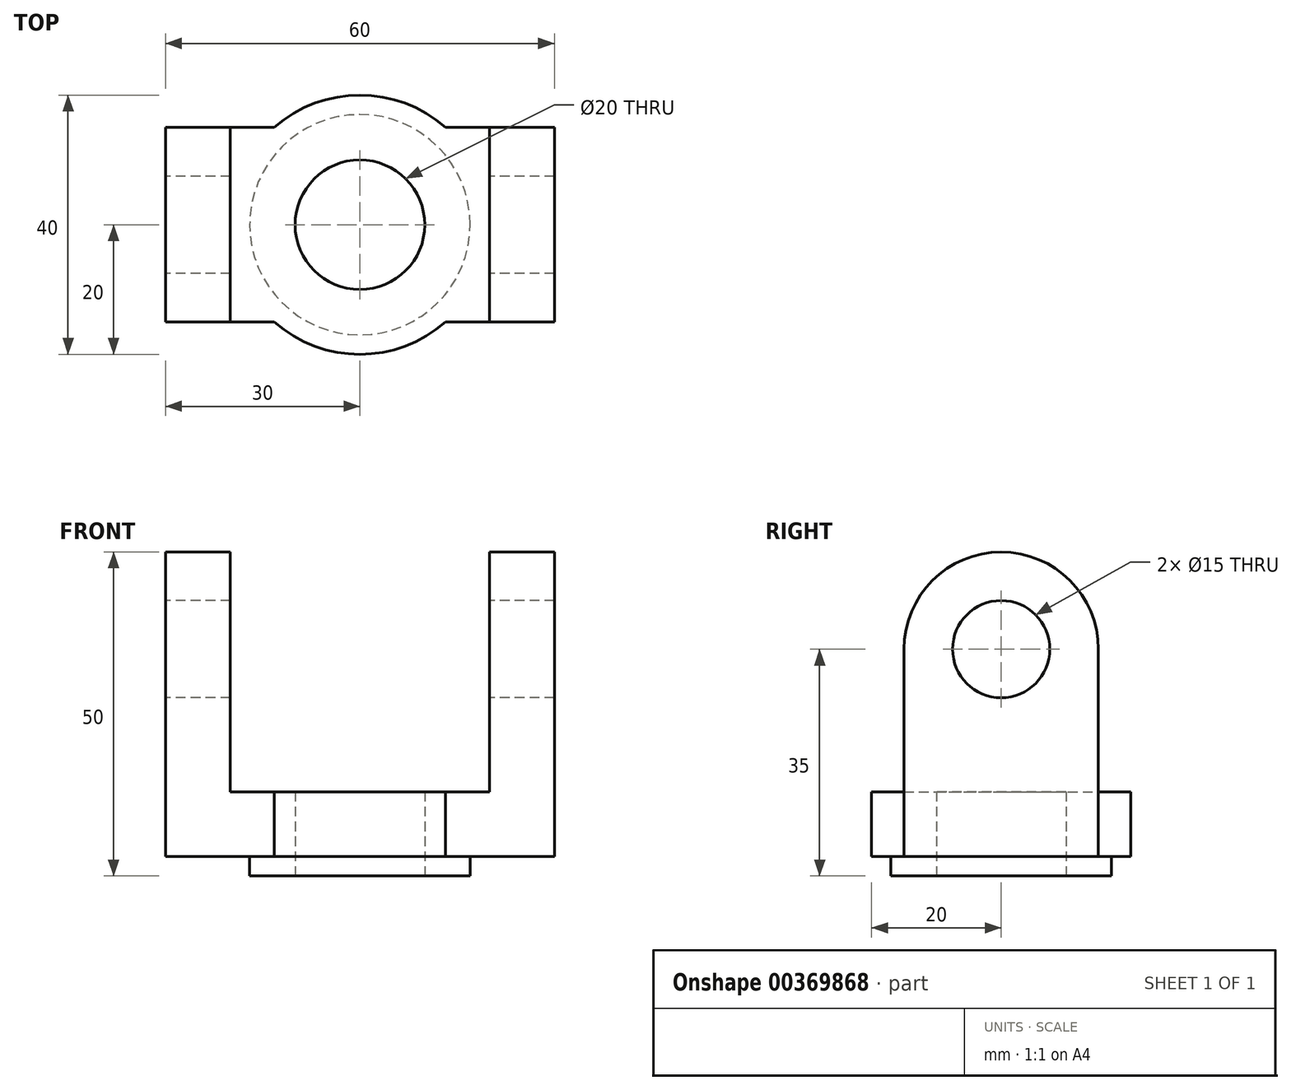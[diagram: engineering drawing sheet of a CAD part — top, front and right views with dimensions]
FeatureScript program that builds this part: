
annotation { "Feature Type Name" : "Feature", "Feature Type Description" : "" }
export const myFeature = defineFeature(function(context is Context, id is Id, definition is map)
    precondition{}
    {
        {
            var Q0;
            Q0=qCreatedBy(makeId("Top.planeOp"),FACE);
            var sketch = newSketch(context, id + "F0", { "sketchPlane" : qUnion([Q0])});
            skLineSegment(sketch, "E0.bottom", {"start": v(-30, 15) * mm, "end": v(-13.23, 15) * mm});
            skLineSegment(sketch, "E0.top", {"start": v(-30, -15) * mm, "end": v(-13.23, -15) * mm});
            skLineSegment(sketch, "E0.left", {"start": v(-30, 15) * mm, "end": v(-30, -15) * mm});
            skLineSegment(sketch, "E0.right", {"start": v(30, 15) * mm, "end": v(30, -15) * mm});
            skPoint(sketch, "E0.middle", {"position": v(0, 0) * mm});
            skCircle(sketch, "E1", {"center": v(0, 0) * mm, "radius": 10 * mm});
            skArc(sketch, "E2", {"start": v(-13.23, -15) * mm, "mid": v(0, -20) * mm, "end": v(13.23, -15) * mm});
            skArc(sketch, "E3.trimOffspring", {"start": v(13.23, 15) * mm, "mid": v(0, 20) * mm, "end": v(-13.23, 15) * mm});
            skLineSegment(sketch, "E4.trimOffspring", {"start": v(13.23, 15) * mm, "end": v(30, 15) * mm});
            skLineSegment(sketch, "E5.trimOffspring", {"start": v(13.23, -15) * mm, "end": v(30, -15) * mm});
            skPoint(sketch, "E6.start.orphan", {"position": v(-20, 15) * mm});
            skPoint(sketch, "E7.start.orphan", {"position": v(20, 15) * mm});
            skCircle(sketch, "E8", {"center": v(0, 0) * mm, "radius": 17 * mm});
            skSolve(sketch);
        }
        {
            var Q0;
            Q0=makeQuery(id+"F0.imprint","IMPRINT",FACE,{"disambiguationData":[TD([[makeQuery(id+"F0.imprint","IMPRINT",EDGE,{"derivedFrom":sQuery(id+"F0.wireOp",EDGE,"E0.bottom")}),-1.0]])]});
            var Q1;
            Q1=makeQuery(id+"F0.imprint","IMPRINT",FACE,{"disambiguationData":[TD([[makeQuery(id+"F0.imprint","IMPRINT",EDGE,{"derivedFrom":sQuery(id+"F0.wireOp",EDGE,"E1")}),-1.0]])]});
            extrude(context, id + "F1", {"entities" : qUnion([Q0, Q1]), "depth" : 10 * mm});
        }
        {
            var Q0;
            Q0=makeQuery(id+"F0.imprint","IMPRINT",FACE,{"disambiguationData":[TD([[makeQuery(id+"F0.imprint","IMPRINT",EDGE,{"derivedFrom":sQuery(id+"F0.wireOp",EDGE,"E1")}),-1.0]])]});
            extrude(context, id + "F2", {"entities" : qUnion([Q0]), "operationType" : NewBodyOperationType.ADD, "oppositeDirection" : true, "depth" : 3 * mm});
        }
        {
            var Q0;
            Q0=qCreatedBy(makeId("Right.planeOp"),FACE);
            var sketch = newSketch(context, id + "F3", { "sketchPlane" : qUnion([Q0])});
            skPoint(sketch, "E9", {"position": v(-15, 10) * mm});
            skPoint(sketch, "E10", {"position": v(15, 10) * mm});
            skLineSegment(sketch, "E11", {"start": v(-15, 10) * mm, "end": v(15, 10) * mm});
            skLineSegment(sketch, "E12", {"start": v(15, 10) * mm, "end": v(15, 32) * mm});
            skLineSegment(sketch, "E13", {"start": v(-15, 10) * mm, "end": v(-15, 32) * mm});
            skArc(sketch, "E14", {"start": v(-15, 32) * mm, "mid": v(0, 47) * mm, "end": v(15, 32) * mm});
            skCircle(sketch, "E15", {"center": v(0, 32) * mm, "radius": 7.5 * mm});
            skSolve(sketch);
        }
        {
            var Q0;
            Q0=makeQuery(id+"F3.imprint","IMPRINT",FACE,{"disambiguationData":[TD([[makeQuery(id+"F3.imprint","IMPRINT",EDGE,{"derivedFrom":sQuery(id+"F3.wireOp",EDGE,"E11")}),1.0]])]});
            extrude(context, id + "F4", {"entities" : qUnion([Q0]), "operationType" : NewBodyOperationType.ADD, "depth" : 60 * mm, "symmetric" : true});
        }
        {
            var Q0;
            Q0=makeQuery(id+"F3.imprint","IMPRINT",FACE,{"disambiguationData":[TD([[makeQuery(id+"F3.imprint","IMPRINT",EDGE,{"derivedFrom":sQuery(id+"F3.wireOp",EDGE,"E11")}),1.0]])]});
            extrude(context, id + "F5", {"entities" : qUnion([Q0]), "operationType" : NewBodyOperationType.REMOVE, "depth" : 40 * mm, "symmetric" : true});
        }
    });
